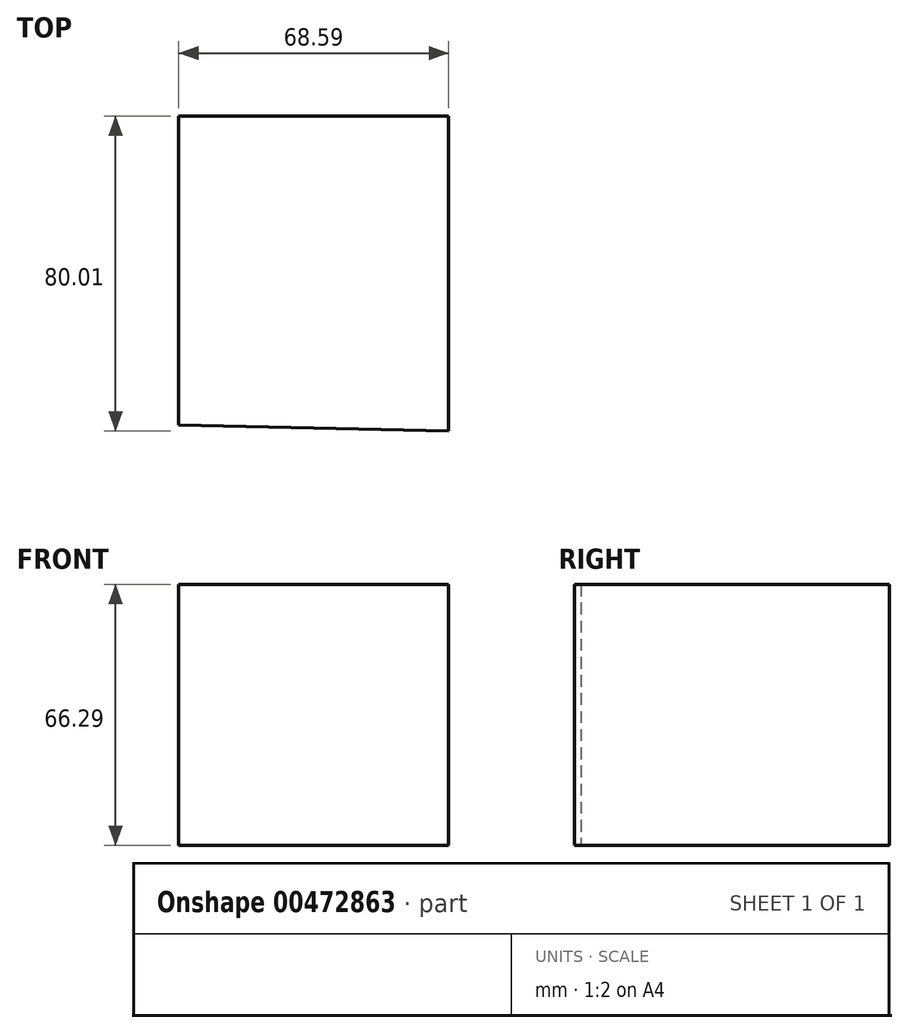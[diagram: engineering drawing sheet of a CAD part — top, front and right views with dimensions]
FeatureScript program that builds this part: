
annotation { "Feature Type Name" : "Feature", "Feature Type Description" : "" }
export const myFeature = defineFeature(function(context is Context, id is Id, definition is map)
    precondition{}
    {
        {
            var Q0;
            Q0=qCreatedBy(makeId("Top.planeOp"),FACE);
            var sketch = newSketch(context, id + "F0", { "sketchPlane" : qUnion([Q0])});
            skLineSegment(sketch, "E0", {"start": v(-43.12, -38.5) * mm, "end": v(-43.12, 39.95) * mm});
            skLineSegment(sketch, "E1", {"start": v(-43.12, 39.95) * mm, "end": v(25.47, 39.95) * mm});
            skLineSegment(sketch, "E2", {"start": v(25.47, 39.95) * mm, "end": v(25.47, -40.06) * mm});
            skLineSegment(sketch, "E3", {"start": v(25.47, -40.06) * mm, "end": v(-43.12, -38.5) * mm});
            skLineSegment(sketch, "E4", {"start": v(0, 0) * mm, "end": v(-10.28, 14.27) * mm});
            skSolve(sketch);
        }
        {
            var Q0;
            Q0=makeQuery(id+"F0.imprint","IMPRINT",FACE,{"disambiguationData":[TD([[makeQuery(id+"F0.imprint","IMPRINT",EDGE,{"derivedFrom":sQuery(id+"F0.wireOp",EDGE,"E0")}),-1.0]])]});
            extrude(context, id + "F1", {"entities" : qUnion([Q0]), "depth" : 66.3 * mm});
        }
    });
